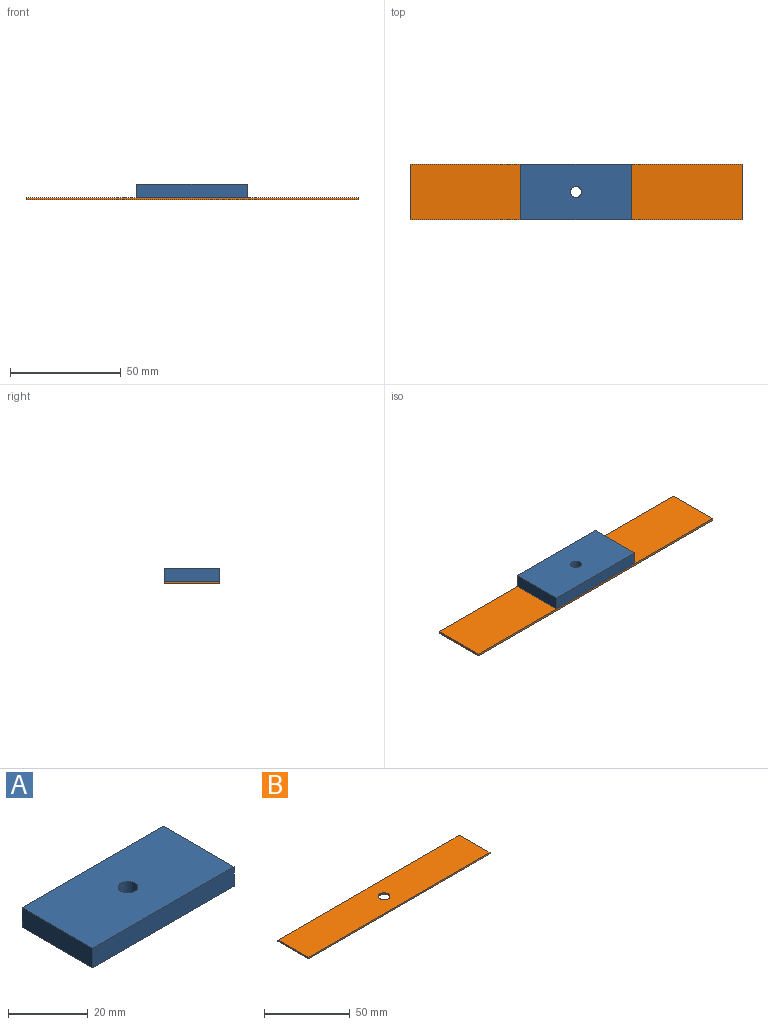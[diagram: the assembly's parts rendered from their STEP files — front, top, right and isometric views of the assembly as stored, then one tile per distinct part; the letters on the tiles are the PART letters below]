
ASSEMBLY  parts=2 mates=1
PART A: 7 faces, bbox 50x25x6 mm
  f0: plane 50x6mm, normal (0,1,0), area 300mm2, adj f1,f3,f4,f5
  f1: plane 25x6mm, normal (-1,0,0), area 150mm2, adj f0,f2,f4,f5
  f2: plane 50x6mm, normal (0,-1,0), area 300mm2, adj f1,f3,f4,f5
  f3: plane 25x6mm, normal (1,0,0), area 150mm2, adj f0,f2,f4,f5
  f4: plane 50x25mm, normal (0,0,1), area 1230.4mm2, adj f0,f1,f2,f3,f6
  f5: plane 50x25mm, normal (0,0,-1), area 1230.4mm2, adj f0,f1,f2,f3,f6
  f6: cylinder r=2.5mm len=6mm, axis (0,0,1), area 94.2mm2, adj f4,f5
PART B: 7 faces, bbox 150x25x1 mm
  f0: plane 150x1mm, normal (0,1,0), area 150mm2, adj f1,f3,f4,f5
  f1: plane 25x1mm, normal (-1,0,0), area 25mm2, adj f0,f2,f4,f5
  f2: plane 150x1mm, normal (0,-1,0), area 150mm2, adj f1,f3,f4,f5
  f3: plane 25x1mm, normal (1,0,0), area 25mm2, adj f0,f2,f4,f5
  f4: plane 150x25mm, normal (0,0,1), area 3711.5mm2, adj f0,f1,f2,f3,f6
  f5: plane 150x25mm, normal (0,0,-1), area 3711.5mm2, adj f0,f1,f2,f3,f6
  f6: cylinder r=3.5mm len=7mm, axis (0,0,1), area 22mm2, adj f4,f5
PLACE A rot(axis=(0,0,1),180deg) t=(100,-25,0)mm
PLACE B t=(0,0,-1)mm
MATE cylindrical A.f6 <-> B.f6  axis (0,0,-1) through (75,-12.5,0)mm
